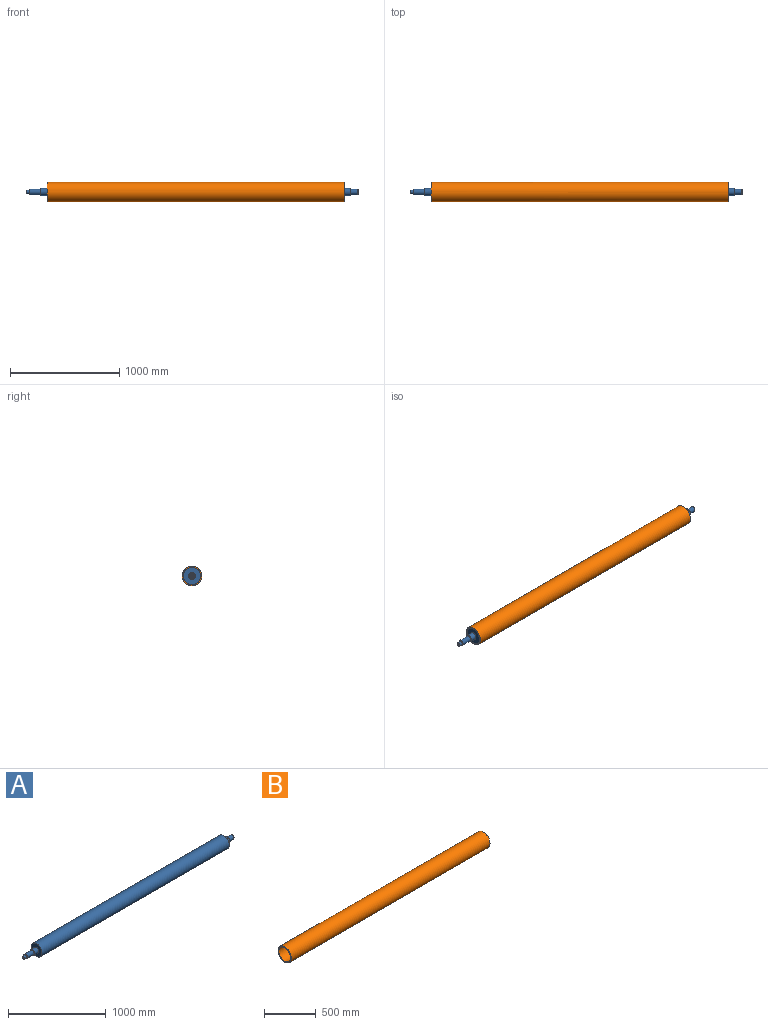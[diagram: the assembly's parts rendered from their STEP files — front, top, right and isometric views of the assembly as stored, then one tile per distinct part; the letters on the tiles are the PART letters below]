
ASSEMBLY  parts=2 mates=1
PART A: 19 faces, bbox 3034x158x158 mm
  f0: cylinder r=79mm len=2714mm, axis (-1,0,0), area 1347152.6mm2, adj f1,f2
  f1: plane 158x158mm, normal (1,0,0), area 16288.4mm2, adj f0,f3
  f2: plane 158x158mm, normal (-1,0,0), area 16288.4mm2, adj f0,f9
  f3: cylinder r=32.5mm len=65mm, axis (-1,0,0), area 11843.8mm2, adj f1,f5
  f4: plane 61x61mm, normal (1,0,0), area 959mm2, adj f5,f6
  f5: cone r=30.5mm half-angle=45deg, axis (-1,0,0), area 559.8mm2, adj f3,f4
  f6: cylinder r=25mm len=63.5mm, axis (-1,0,0), area 9974.6mm2, adj f4,f8
  f7: plane 47x47mm, normal (1,0,0), area 1656.4mm2, adj f8,f18
  f8: cone r=23.5mm half-angle=45deg, axis (-1,0,0), area 323.2mm2, adj f6,f7
  f9: cylinder r=32.5mm len=65mm, axis (1,0,0), area 11843.8mm2, adj f2,f15
  f10: plane 61x61mm, normal (-1,0,0), area 959mm2, adj f11,f15
  f11: cylinder r=25mm len=98.5mm, axis (1,0,0), area 15472.3mm2, adj f10,f17
  f12: plane 47x47mm, normal (-1,0,0), area 772.8mm2, adj f13,f17
  f13: cylinder r=17.5mm len=35mm, axis (1,0,0), area 3683.5mm2, adj f12,f16
  f14: plane 32x32mm, normal (-1,0,0), area 725.7mm2, adj f16,f18
  f15: cone r=30.5mm half-angle=45deg, axis (1,0,0), area 559.8mm2, adj f9,f10
  f16: cone r=16mm half-angle=45deg, axis (1,0,0), area 223.3mm2, adj f13,f14
  f17: cone r=23.5mm half-angle=45deg, axis (1,0,0), area 323.2mm2, adj f11,f12
  f18: cylinder r=5mm len=3034mm, axis (1,0,0), area 95315.9mm2, adj f7,f14
PART B: 4 faces, bbox 2714x180x180 mm
  f0: plane 180x180mm, normal (-1,0,0), area 5840.2mm2, adj f1,f2
  f1: cylinder r=79mm len=2714mm, axis (1,0,0), area 1347152.6mm2, adj f0,f3
  f2: cylinder r=90mm len=2714mm, axis (1,0,0), area 1534730.8mm2, adj f0,f3
  f3: plane 180x180mm, normal (1,0,0), area 5840.2mm2, adj f1,f2
PLACE A t=(-124.09,-14.3,116.33)mm
PLACE B t=(-124.09,-14.3,116.33)mm
MATE fastened B.f1 <-> A.f0  axis (1,0,0) through (1232.91,-14.3,116.33)mm
